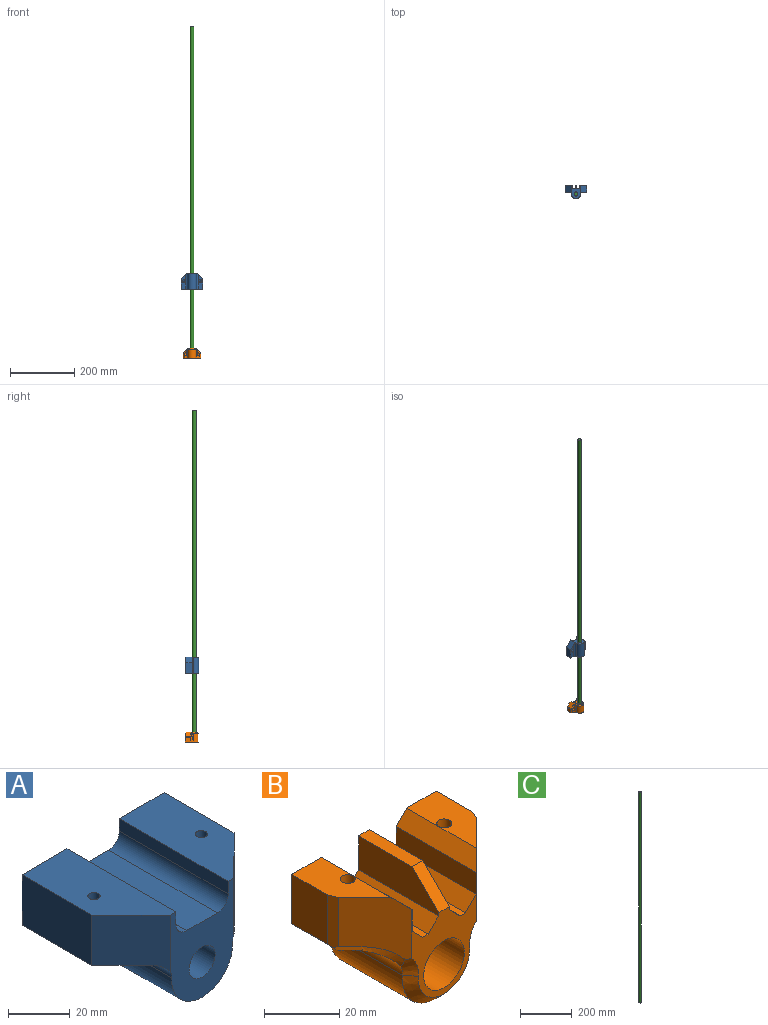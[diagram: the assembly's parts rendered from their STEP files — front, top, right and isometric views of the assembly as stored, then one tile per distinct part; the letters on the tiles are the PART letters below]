
ASSEMBLY  parts=3 mates=2
PART A: 25 faces, bbox 65.3x50x40 mm
  f0: plane 50x20.65mm, normal (0,0,1), area 857.9mm2, adj f1,f5,f11,f15,f19,f23
  f1: plane 40x29.3mm, normal (0,-1,0), area 723.6mm2, adj f0,f4,f7,f10,f12,f13,f18,f19
  f2: cone r=0mm half-angle=59deg, axis (0,0,-1), area 77mm2, adj f16,f17
  f3: cone r=0mm half-angle=59deg, axis (0,0,-1), area 77mm2, adj f14,f15
  f4: plane 50x20.65mm, normal (0,0,1), area 857.9mm2, adj f1,f9,f11,f17,f18,f24
  f5: plane 32x20mm, normal (-1,0,0), area 640mm2, adj f0,f6,f11,f23
  f6: plane 45.68x13.68mm, normal (0,0,-1), area 452.6mm2, adj f5,f11,f12,f14,f23
  f7: cylinder r=14mm len=50mm, axis (0,1,0), area 2272.8mm2, adj f1,f11,f12,f13
  f8: plane 45.68x13.68mm, normal (0,0,-1), area 452.6mm2, adj f9,f11,f13,f16,f24
  f9: plane 32x20mm, normal (1,0,0), area 640mm2, adj f4,f8,f11,f24
  f10: cylinder r=6mm len=50mm, axis (0,1,0), area 1885mm2, adj f1,f11
  f11: plane 65.3x40mm, normal (0,1,0), area 1449.9mm2, adj f0,f4,f5,f6,f7,f8,f9,f10
  f12: cylinder r=5mm len=50mm, axis (0,1,0), area 395.7mm2, adj f1,f6,f7,f11,f23
  f13: cylinder r=5mm len=50mm, axis (0,1,0), area 395.7mm2, adj f1,f7,f8,f11,f24
  f14: cylinder r=5mm len=10mm, axis (0,0,-1), area 314.2mm2, adj f3,f6
  f15: cylinder r=2mm len=8.2mm, axis (0,0,-1), area 103mm2, adj f0,f3
  f16: cylinder r=5mm len=10mm, axis (0,0,-1), area 314.2mm2, adj f2,f8
  f17: cylinder r=2mm len=8.2mm, axis (0,0,-1), area 103mm2, adj f2,f4
  f18: plane 50x5mm, normal (-1,0,0), area 250mm2, adj f1,f4,f11,f21
  f19: plane 50x5mm, normal (1,0,0), area 250mm2, adj f0,f1,f11,f22
  f20: plane 50x14mm, normal (0,0,1), area 700mm2, adj f1,f11,f21,f22
  f21: cylinder r=5mm len=50mm, axis (0,1,0), area 392.7mm2, adj f1,f11,f18,f20
  f22: cylinder r=5mm len=50mm, axis (0,-1,0), area 392.7mm2, adj f1,f11,f19,f20
  f23: plane 22.49x18mm, normal (-0.71,-0.71,0), area 513.5mm2, adj f0,f1,f5,f6,f12
  f24: plane 22.49x18mm, normal (0.71,-0.71,0), area 513.5mm2, adj f1,f4,f8,f9,f13
PART B: 50 faces, bbox 55.2x31x41.3 mm
  f0: plane 1.11x1.11mm, normal (0,0,-1), area 0.5mm2, adj f17,f21,f44
  f1: plane 1.61x0.27mm, normal (0,0,-1), area 0.1mm2, adj f19,f38,f42
  f2: plane 1.61x0.27mm, normal (0,0,-1), area 0.1mm2, adj f17,f40,f44
  f3: plane 12x4.5mm, normal (0,0,-1), area 36.8mm2, adj f16,f19,f22,f38
  f4: plane 26.07x11.07mm, normal (0,0,1), area 213.9mm2, adj f10,f16,f18,f30,f35,f41
  f5: plane 20x4mm, normal (0,0,1), area 80mm2, adj f16,f25,f28,f49
  f6: plane 33.37x24.15mm, normal (0,-1,0), area 292.1mm2, adj f15,f24,f25,f26,f27,f28,f29,f30
  f7: cone r=0mm half-angle=59deg, axis (0,0,-1), area 77mm2, adj f19,f20
  f8: cone r=0mm half-angle=59deg, axis (0,0,-1), area 77mm2, adj f17,f18
  f9: plane 26.07x11.07mm, normal (0,0,1), area 213.9mm2, adj f14,f16,f20,f31,f34,f39
  f10: plane 16x13.34mm, normal (-1,0,0), area 213.5mm2, adj f4,f16,f40,f41
  f11: plane 12x4.5mm, normal (0,0,-1), area 36.8mm2, adj f16,f17,f21,f40
  f12: cylinder r=12.65mm len=27mm, axis (0,1,0), area 1133.5mm2, adj f16,f21,f22,f47
  f13: plane 1.11x1.11mm, normal (0,0,-1), area 0.5mm2, adj f19,f22,f42
  f14: plane 16x13.34mm, normal (1,0,0), area 213.5mm2, adj f9,f16,f38,f39
  f15: cylinder r=7.65mm len=24mm, axis (0,1,0), area 1153.6mm2, adj f6,f23
  f16: plane 54.15x40.3mm, normal (0,1,0), area 1242.4mm2, adj f3,f4,f5,f9,f10,f11,f12,f14
  f17: cylinder r=5mm len=13.61mm, axis (0,0,-1), area 340.8mm2, adj f0,f2,f8,f11,f21,f44
  f18: cylinder r=2mm len=8.2mm, axis (0,0,-1), area 103mm2, adj f4,f8
  f19: cylinder r=5mm len=13.61mm, axis (0,0,-1), area 344.3mm2, adj f1,f3,f7,f13,f22,f42
  f20: cylinder r=2mm len=8.2mm, axis (0,0,-1), area 103mm2, adj f7,f9
  f21: cylinder r=6mm len=27mm, axis (0,1,0), area 189.1mm2, adj f0,f11,f12,f16,f17,f45,f48
  f22: cylinder r=6mm len=27mm, axis (0,1,0), area 189.1mm2, adj f3,f12,f13,f16,f19,f43,f46
  f23: plane 15.3x15.3mm, normal (0,-1,0), area 183.9mm2, adj f15
  f24: plane 30x7mm, normal (-1,0,0), area 210mm2, adj f6,f16,f34,f37
  f25: plane 30x11mm, normal (1,0,0), area 280mm2, adj f5,f6,f16,f33,f49
  f26: plane 30x2mm, normal (0,0,1), area 60mm2, adj f6,f16,f33,f37
  f27: plane 30x7mm, normal (1,0,0), area 210mm2, adj f6,f16,f35,f36
  f28: plane 30x11mm, normal (-1,0,0), area 280mm2, adj f5,f6,f16,f32,f49
  f29: plane 30x2mm, normal (0,0,1), area 60mm2, adj f6,f16,f32,f36
  f30: plane 20.33x13.85mm, normal (-0.71,-0.71,0), area 323.2mm2, adj f4,f6,f35,f41,f44,f45,f48
  f31: plane 20.33x13.85mm, normal (0.71,-0.71,0), area 323.2mm2, adj f6,f9,f34,f39,f42,f43,f46
  f32: plane 30x4mm, normal (-0.71,0,0.71), area 169.7mm2, adj f6,f16,f28,f29
  f33: plane 30x4mm, normal (0.71,0,0.71), area 169.7mm2, adj f6,f16,f25,f26
  f34: plane 30x4mm, normal (-0.71,0,0.71), area 158.8mm2, adj f6,f9,f16,f24,f31
  f35: plane 30x4mm, normal (0.71,0,0.71), area 158.8mm2, adj f4,f6,f16,f27,f30
  f36: plane 30x4mm, normal (0.71,0,0.71), area 169.7mm2, adj f6,f16,f27,f29
  f37: plane 30x4mm, normal (-0.71,0,0.71), area 169.7mm2, adj f6,f16,f24,f26
  f38: plane 14.76x4mm, normal (0.71,0,-0.71), area 79.5mm2, adj f1,f3,f14,f16,f39,f42
  f39: plane 16.59x2.83mm, normal (0.92,-0.38,0), area 49.9mm2, adj f9,f14,f31,f38,f42
  f40: plane 14.76x4mm, normal (-0.71,0,-0.71), area 79.5mm2, adj f2,f10,f11,f16,f41,f44
  f41: plane 16.59x2.83mm, normal (-0.92,-0.38,0), area 49.9mm2, adj f4,f10,f30,f40,f44
  f42: plane 8.94x8.36mm, normal (0.5,-0.5,-0.71), area 37.8mm2, adj f1,f13,f19,f31,f38,f39,f43
  f43: bspline ~11.99x9.16mm, area 55.8mm2, adj f22,f31,f42,f46
  f44: plane 8.94x8.36mm, normal (-0.5,-0.5,-0.71), area 37.8mm2, adj f0,f2,f17,f30,f40,f41,f45
  f45: bspline ~11.99x9.16mm, area 55.8mm2, adj f21,f30,f44,f48
  f46: cone r=9mm half-angle=45deg, axis (0,-1,0), area 25mm2, adj f6,f22,f31,f43,f47
  f47: cone r=9.65mm half-angle=45deg, axis (0,1,0), area 157mm2, adj f6,f12,f46,f48
  f48: cone r=9mm half-angle=45deg, axis (0,-1,0), area 25mm2, adj f6,f21,f30,f45,f47
  f49: plane 10x10mm, normal (0,-0.71,0.71), area 56.6mm2, adj f5,f6,f25,f28
PART C: 3 faces, bbox 11.4x11.4x1000 mm
  f0: cylinder r=5.7mm len=1000mm, axis (0,0,-1), area 35814.2mm2, adj f1,f2
  f1: plane 11.4x11.4mm, normal (0,0,1), area 102.1mm2, adj f0
  f2: plane 11.4x11.4mm, normal (0,0,-1), area 102.1mm2, adj f0
PLACE A rot(axis=(-1,0,0),90deg) t=(-289.02,-47.48,204.03)mm
PLACE B rot(axis=(-1,0,0),90deg) t=(-289.02,-47.48,-9.52)mm
PLACE C t=(-289.02,-47.48,20.48)mm
MATE slider C.f0 <-> A.f10  axis (0,0,-1) through (-289.02,-47.48,520.48)mm
MATE fastened B.f15 <-> C.f0  axis (0,0,1) through (-289.02,-47.48,20.48)mm
